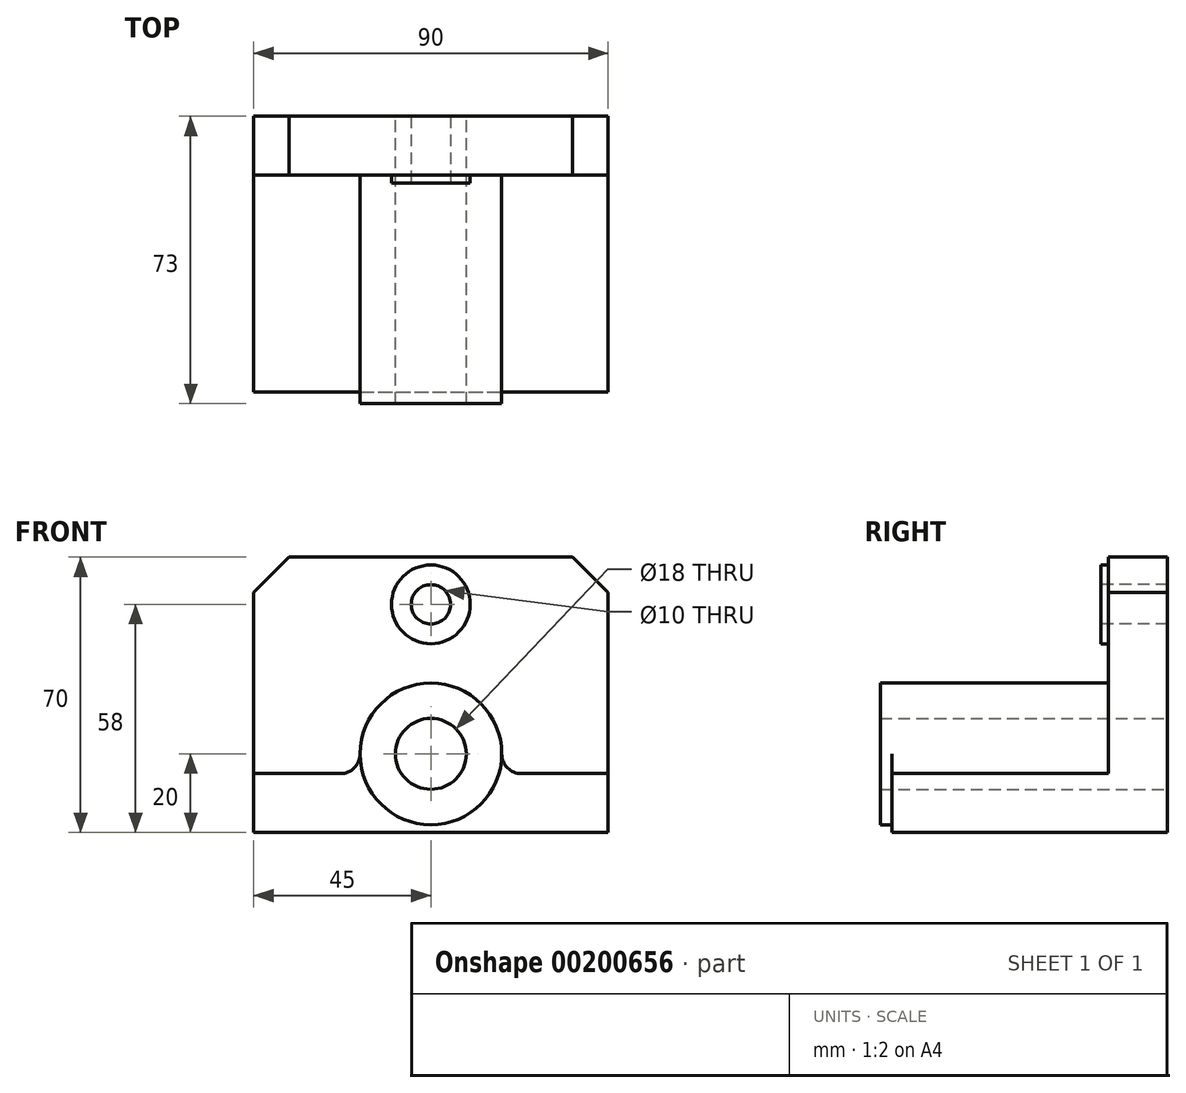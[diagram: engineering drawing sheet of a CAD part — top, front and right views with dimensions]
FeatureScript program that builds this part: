
annotation { "Feature Type Name" : "Feature", "Feature Type Description" : "" }
export const myFeature = defineFeature(function(context is Context, id is Id, definition is map)
    precondition{}
    {
        {
            var Q0;
            Q0=qCreatedBy(makeId("Front.planeOp"),FACE);
            var sketch = newSketch(context, id + "F0", { "sketchPlane" : qUnion([Q0])});
            skCircle(sketch, "E0", {"center": v(0, 0) * mm, "radius": 18 * mm});
            skCircle(sketch, "E1", {"center": v(0, 0) * mm, "radius": 9 * mm});
            skLineSegment(sketch, "E2", {"start": v(-45, -20) * mm, "end": v(45, -20) * mm});
            skLineSegment(sketch, "E3", {"start": v(-45, -20) * mm, "end": v(-45, -5) * mm});
            skLineSegment(sketch, "E4", {"start": v(45, -20) * mm, "end": v(45, -5) * mm});
            skLineSegment(sketch, "E5", {"start": v(-45, -5) * mm, "end": v(-17.3, -5) * mm});
            skLineSegment(sketch, "E6", {"start": v(45, -5) * mm, "end": v(17.3, -5) * mm});
            skLineSegment(sketch, "E7", {"start": v(0, 0) * mm, "end": v(0, -20) * mm});
            skSolve(sketch);
        }
        {
            var Q0;
            {var subQ1=sQuery(id+"F0.wireOp",EDGE,"E4");Q0=makeQuery(id+"F0.imprint","IMPRINT",FACE,{"disambiguationData":[TD([[makeQuery(id+"F0.imprint","IMPRINT",EDGE,{"derivedFrom":subQ1}),1.0]])]});}
            var Q1;
            Q1=makeQuery(id+"F0.imprint","IMPRINT",FACE,{"disambiguationData":[TD([[makeQuery(id+"F0.imprint","IMPRINT",EDGE,{"derivedFrom":sQuery(id+"F0.wireOp",EDGE,"E1")}),-1.0]])]});
            var Q2;
            {var subQ1=sQuery(id+"F0.wireOp",EDGE,"E3");Q2=makeQuery(id+"F0.imprint","IMPRINT",FACE,{"disambiguationData":[TD([[makeQuery(id+"F0.imprint","IMPRINT",EDGE,{"derivedFrom":subQ1}),-1.0]])]});}
            extrude(context, id + "F1", {"entities" : qUnion([Q0, Q1, Q2]), "depth" : 70 * mm});
        }
        {
            var Q0;
            Q0=makeQuery(id+"F1.opExtrude","SWEPT_EDGE",EDGE,{"disambiguationData":[OSD([sQuery(id+"F0.wireOp",EDGE,"E0"),sQuery(id+"F0.wireOp",EDGE,"E5")])]});
            fillet(context, id + "F2", {"entities" : qUnion([Q0]), "radius" : 5 * mm, "tangentPropagation" : true, "allowEdgeOverflow" : false});
        }
        {
            var Q0;
            Q0=makeQuery(id+"F1.opExtrude","SWEPT_EDGE",EDGE,{"disambiguationData":[OSD([sQuery(id+"F0.wireOp",EDGE,"E0"),sQuery(id+"F0.wireOp",EDGE,"E6")])]});
            fillet(context, id + "F3", {"entities" : qUnion([Q0]), "radius" : 5 * mm, "tangentPropagation" : true, "allowEdgeOverflow" : false});
        }
        {
            var Q0;
            Q0=qCreatedBy(makeId("Front.planeOp"),FACE);
            var sketch = newSketch(context, id + "F4", { "sketchPlane" : qUnion([Q0])});
            skLineSegment(sketch, "E8", {"start": v(45, -5) * mm, "end": v(45, 50) * mm});
            skLineSegment(sketch, "E9", {"start": v(45, 50) * mm, "end": v(-45, 50) * mm});
            skLineSegment(sketch, "E10", {"start": v(-45, 50) * mm, "end": v(-45, -5) * mm});
            skLineSegment(sketch, "E11.0", {"start": v(45, -5) * mm, "end": v(23, -5) * mm});
            skArc(sketch, "E12.0", {"start": v(18, 0) * mm, "mid": v(19.46, -3.54) * mm, "end": v(23, -5) * mm});
            skArc(sketch, "E13.0", {"start": v(18, 0) * mm, "mid": v(0, 18) * mm, "end": v(-18, 0) * mm});
            skArc(sketch, "E14.0", {"start": v(-23, -5) * mm, "mid": v(-19.46, -3.54) * mm, "end": v(-18, 0) * mm});
            skLineSegment(sketch, "E15.0", {"start": v(-45, -5) * mm, "end": v(-23, -5) * mm});
            skSolve(sketch);
        }
        {
            var Q0;
            Q0=makeQuery(id+"F4.imprint","IMPRINT",FACE,{"disambiguationData":[TD([[makeQuery(id+"F4.imprint","IMPRINT",EDGE,{"derivedFrom":sQuery(id+"F4.wireOp",EDGE,"E8")}),1.0]])]});
            extrude(context, id + "F5", {"entities" : qUnion([Q0]), "operationType" : NewBodyOperationType.ADD, "depth" : 15 * mm});
        }
        {
            var Q0;
            Q0=makeQuery(id+"F5.opExtrude","SWEPT_EDGE",EDGE,{"disambiguationData":[OSD([sQuery(id+"F4.wireOp",EDGE,"E8"),sQuery(id+"F4.wireOp",EDGE,"E9")])]});
            var Q1;
            Q1=makeQuery(id+"F5.opExtrude","SWEPT_EDGE",EDGE,{"disambiguationData":[OSD([sQuery(id+"F4.wireOp",EDGE,"E9"),sQuery(id+"F4.wireOp",EDGE,"E10")])]});
            chamfer(context, id + "F6", {"entities" : qUnion([Q0, Q1]), "width" : 9 * mm, "tangentPropagation" : true});
        }
        {
            var Q0;
            Q0=makeQuery(id+"F1.opExtrude","CAP_FACE",FACE,{"disambiguationData":[OSD([sQuery(id+"F0.wireOp",EDGE,"E0"),sQuery(id+"F0.wireOp",EDGE,"E1"),sQuery(id+"F0.wireOp",EDGE,"E2"),sQuery(id+"F0.wireOp",EDGE,"E3"),sQuery(id+"F0.wireOp",EDGE,"E4"),sQuery(id+"F0.wireOp",EDGE,"E5"),sQuery(id+"F0.wireOp",EDGE,"E6")])],"isStart":false});
            var sketch = newSketch(context, id + "F7", { "sketchPlane" : qUnion([Q0])});
            skCircle(sketch, "E16", {"center": v(0, 0) * mm, "radius": 18 * mm});
            skCircle(sketch, "E17", {"center": v(0, 0) * mm, "radius": 9 * mm});
            skSolve(sketch);
        }
        {
            var Q0;
            Q0=makeQuery(id+"F7.imprint","IMPRINT",FACE,{"disambiguationData":[TD([[makeQuery(id+"F7.imprint","IMPRINT",EDGE,{"derivedFrom":sQuery(id+"F7.wireOp",EDGE,"E17")}),-1.0]])]});
            extrude(context, id + "F8", {"entities" : qUnion([Q0]), "operationType" : NewBodyOperationType.ADD, "depth" : 3 * mm});
        }
        {
            var Q0;
            Q0=makeQuery(id+"F5.opExtrude","CAP_FACE",FACE,{"disambiguationData":[OSD([sQuery(id+"F4.wireOp",EDGE,"E8"),sQuery(id+"F4.wireOp",EDGE,"E9"),sQuery(id+"F4.wireOp",EDGE,"E10"),sQuery(id+"F4.wireOp",EDGE,"E11.0"),sQuery(id+"F4.wireOp",EDGE,"E12.0"),sQuery(id+"F4.wireOp",EDGE,"E13.0"),sQuery(id+"F4.wireOp",EDGE,"E14.0"),sQuery(id+"F4.wireOp",EDGE,"E15.0")])],"isStart":false});
            var sketch = newSketch(context, id + "F9", { "sketchPlane" : qUnion([Q0])});
            skCircle(sketch, "E18", {"center": v(0, 38) * mm, "radius": 10 * mm});
            skCircle(sketch, "E19", {"center": v(0, 38) * mm, "radius": 5 * mm});
            skSolve(sketch);
        }
        {
            var Q0;
            Q0=makeQuery(id+"F9.imprint","IMPRINT",FACE,{"disambiguationData":[TD([[makeQuery(id+"F9.imprint","IMPRINT",EDGE,{"derivedFrom":sQuery(id+"F9.wireOp",EDGE,"E19")}),1.0]])]});
            extrude(context, id + "F10", {"entities" : qUnion([Q0]), "operationType" : NewBodyOperationType.REMOVE, "oppositeDirection" : true, "depth" : 25 * mm});
        }
        {
            var Q0;
            Q0=makeQuery(id+"F5.opExtrude","CAP_FACE",FACE,{"disambiguationData":[OSD([sQuery(id+"F4.wireOp",EDGE,"E8"),sQuery(id+"F4.wireOp",EDGE,"E9"),sQuery(id+"F4.wireOp",EDGE,"E10"),sQuery(id+"F4.wireOp",EDGE,"E11.0"),sQuery(id+"F4.wireOp",EDGE,"E12.0"),sQuery(id+"F4.wireOp",EDGE,"E13.0"),sQuery(id+"F4.wireOp",EDGE,"E14.0"),sQuery(id+"F4.wireOp",EDGE,"E15.0")])],"isStart":false});
            var sketch = newSketch(context, id + "F11", { "sketchPlane" : qUnion([Q0])});
            skCircle(sketch, "E20", {"center": v(0, 38) * mm, "radius": 10 * mm});
            skSolve(sketch);
        }
        {
            var Q0;
            Q0=makeQuery(id+"F11.imprint","IMPRINT",FACE,{"disambiguationData":[TD([[makeQuery(id+"F11.imprint","IMPRINT",EDGE,{"derivedFrom":sQuery(id+"F11.wireOp",EDGE,"E20")}),1.0]])]});
            extrude(context, id + "F12", {"entities" : qUnion([Q0]), "operationType" : NewBodyOperationType.ADD, "depth" : 2 * mm});
        }
        {
            var Q0;
            Q0=makeQuery(id+"F8.opExtrude","CAP_FACE",FACE,{"disambiguationData":[OSD([sQuery(id+"F7.wireOp",EDGE,"E16"),sQuery(id+"F7.wireOp",EDGE,"E17")])],"isStart":false});
            var sketch = newSketch(context, id + "F13", { "sketchPlane" : qUnion([Q0])});
            skPoint(sketch, "E21", {"position": v(0, 0) * mm});
            skCircle(sketch, "E22.0", {"center": v(0, 0) * mm, "radius": 18 * mm, "construction": true});
            skLineSegment(sketch, "E23", {"start": v(0, 0) * mm, "end": v(49.26, 55.34) * mm, "construction": true});
            skPoint(sketch, "E24", {"position": v(11.97, 13.45) * mm});
            skSolve(sketch);
        }
    });
